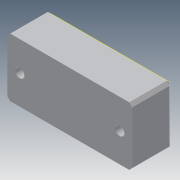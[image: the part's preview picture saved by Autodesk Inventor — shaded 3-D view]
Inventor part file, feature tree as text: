
AUTODESK INVENTOR PART (.ipt)
format: ipt  version: 2014 (Build 180170000, 170)  size: 96,768 bytes
history: native  units: in
note: dims shown in document units (in); Inventor stores cm internally (conversion verified against a paired STEP export)
features: sketch x3, extrude x1, hole x1, chamfer x1
ambient origin geometry x8: Origin, YZ Plane, XZ Plane, XY Plane, X Axis, Y Axis, Z Axis, Center Point
bodies: Solid1 (feature_tree)
feature tree (6):
  extrude  "Extrusion1"  Depth=1.17in
  hole  "Hole1"  [1 undecoded]
  chamfer  "Chamfer1"  Distance=0.06in Angle=45.0deg
  sketch  "Sketch3"  dims[d5=0.1875in d6=0.75in d7=0.375in d8=0.25in d9=0.5635in d10=1.0in d11=0.8108in d12=0.06in d13=0.125in d14=45.0deg]
  sketch  "Sketch1"  dims[d0=2.5in d1=1.17in]
  sketch  "Sketch2"  dims[d2=0.8125in d3=0.0in d4=2.0in]
note: 1 required parameter value undecoded (feature->parameter linkage not recoverable at this tier; creation-order binding heuristic only, values carry confidence <= 0.55)
